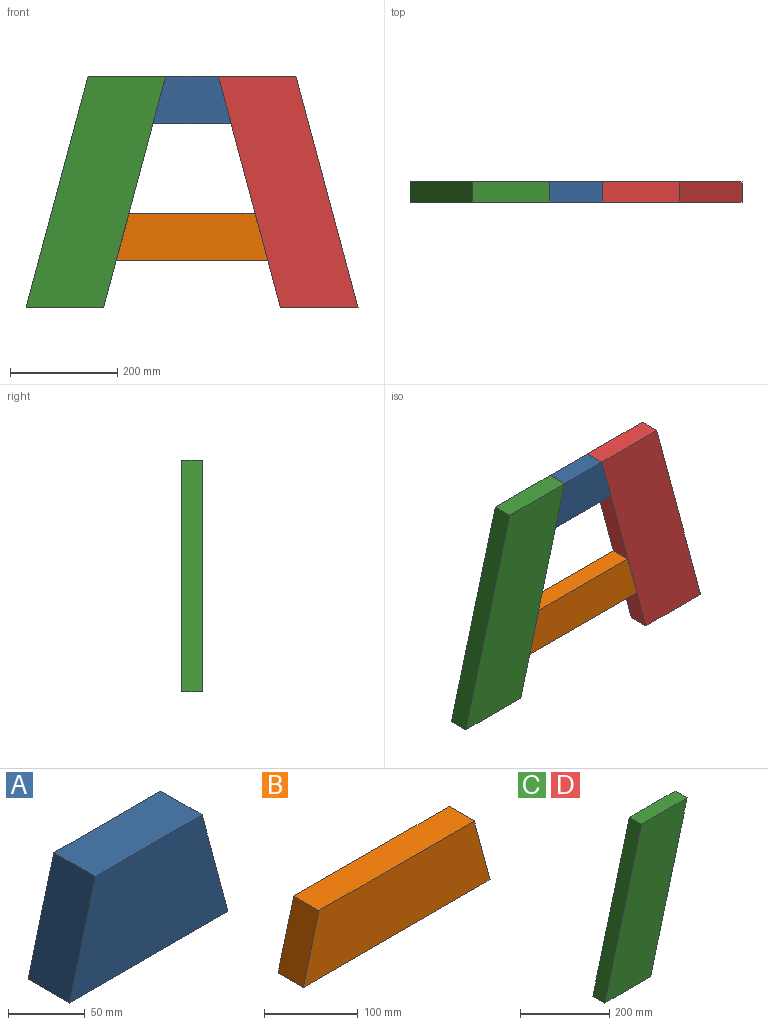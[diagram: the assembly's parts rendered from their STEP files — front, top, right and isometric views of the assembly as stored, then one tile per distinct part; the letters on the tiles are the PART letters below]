
ASSEMBLY  parts=4 mates=3
PART A: 6 faces, bbox 146.1x38.1x88.9 mm
  f0: plane 88.9x38.1mm, normal (-0.97,0,0.26), area 3506.6mm2, adj f1,f3,f4,f5
  f1: plane 146.05x38.1mm, normal (0,0,-1), area 5564.5mm2, adj f0,f2,f4,f5
  f2: plane 88.9x38.1mm, normal (0.97,0,0.26), area 3506.6mm2, adj f1,f3,f4,f5
  f3: plane 98.41x38.1mm, normal (0,0,1), area 3749.4mm2, adj f0,f2,f4,f5
  f4: plane 146.05x88.9mm, normal (0,-1,0), area 10866.2mm2, adj f0,f1,f2,f3
  f5: plane 146.05x88.9mm, normal (0,1,0), area 10866.2mm2, adj f0,f1,f2,f3
PART B: 6 faces, bbox 282.6x38.1x88.9 mm
  f0: plane 88.9x38.1mm, normal (-0.97,0,0.26), area 3506.6mm2, adj f1,f3,f4,f5
  f1: plane 282.58x38.1mm, normal (0,0,-1), area 10766.1mm2, adj f0,f2,f4,f5
  f2: plane 88.9x38.1mm, normal (0.97,0,0.26), area 3506.6mm2, adj f1,f3,f4,f5
  f3: plane 234.93x38.1mm, normal (0,0,1), area 8951mm2, adj f0,f2,f4,f5
  f4: plane 282.58x88.9mm, normal (0,-1,0), area 23003.3mm2, adj f0,f1,f2,f3
  f5: plane 282.58x88.9mm, normal (0,1,0), area 23003.3mm2, adj f0,f1,f2,f3
PART C: 6 faces, bbox 260.3x38.1x431.8 mm
  f0: plane 431.8x115.7mm, normal (-0.97,0,0.26), area 17031.9mm2, adj f1,f3,f4,f5
  f1: plane 144.63x38.1mm, normal (0,0,-1), area 5510.3mm2, adj f0,f2,f4,f5
  f2: plane 431.8x115.7mm, normal (0.97,0,-0.26), area 17031.9mm2, adj f1,f3,f4,f5
  f3: plane 144.63x38.1mm, normal (0,0,1), area 5510.3mm2, adj f0,f2,f4,f5
  f4: plane 431.8x260.33mm, normal (0,-1,0), area 62450.4mm2, adj f0,f1,f2,f3
  f5: plane 431.8x260.33mm, normal (0,1,0), area 62450.4mm2, adj f0,f1,f2,f3
PART D: same geometry as C
PLACE A t=(164.19,19.05,342.9)mm
PLACE B t=(96.08,19.05,87.59)mm
PLACE C t=(-72.31,19.05,0)mm
PLACE D rot(axis=(0,0,-1),180deg) t=(546.75,-19.05,0)mm
MATE fastened D.f2 <-> B.f2  axis (-0.97,0,-0.26) through (402.12,0,0)mm
MATE fastened C.f2 <-> A.f0  axis (0.97,0,-0.26) through (188.01,0,431.8)mm
MATE fastened A.f2 <-> D.f2  axis (0.97,0,0.26) through (286.42,0,431.8)mm
